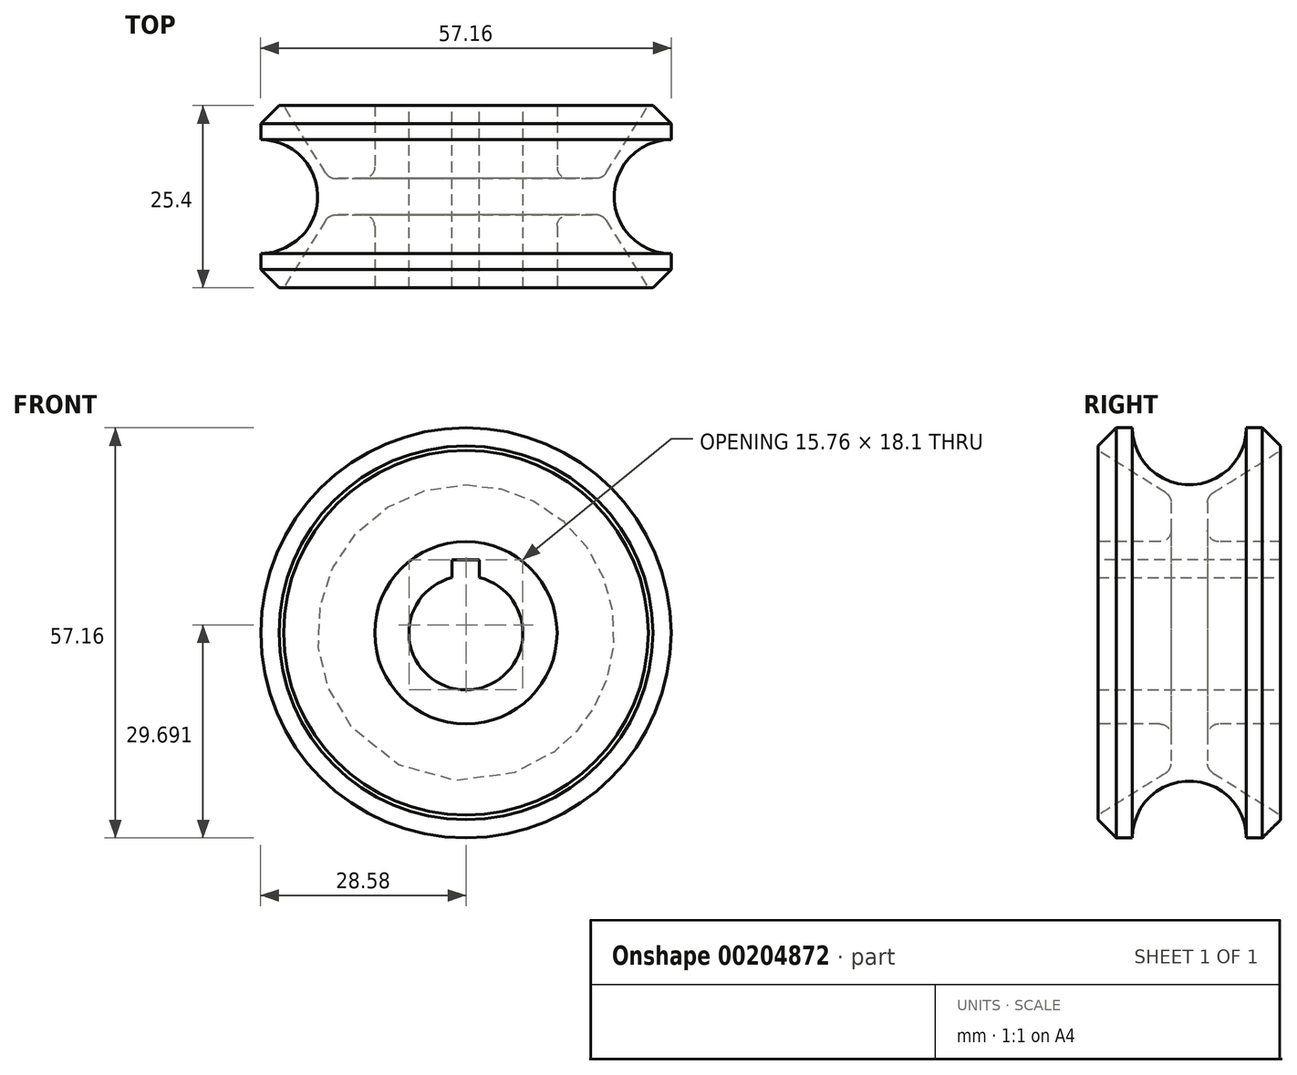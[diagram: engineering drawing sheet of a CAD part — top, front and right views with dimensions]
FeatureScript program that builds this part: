
annotation { "Feature Type Name" : "Feature", "Feature Type Description" : "" }
export const myFeature = defineFeature(function(context is Context, id is Id, definition is map)
    precondition{}
    {
        {
            var Q0;
            Q0=qCreatedBy(makeId("Front.planeOp"),FACE);
            var sketch = newSketch(context, id + "F0", { "sketchPlane" : qUnion([Q0])});
            skCircle(sketch, "E0", {"center": v(0, 0) * mm, "radius": 7.94 * mm});
            skCircle(sketch, "E1", {"center": v(0, 0) * mm, "radius": 28.58 * mm});
            skSolve(sketch);
        }
        {
            var Q0;
            Q0=makeQuery(id+"F0.imprint","IMPRINT",FACE,{"disambiguationData":[TD([[makeQuery(id+"F0.imprint","IMPRINT",EDGE,{"derivedFrom":sQuery(id+"F0.wireOp",EDGE,"E0")}),-1.0]])]});
            extrude(context, id + "F1", {"entities" : qUnion([Q0]), "endBound" : BoundingType.SYMMETRIC, "depth" : 25.4 * mm});
        }
        {
            var Q0;
            Q0=qCreatedBy(makeId("Right.planeOp"),FACE);
            var sketch = newSketch(context, id + "F2", { "sketchPlane" : qUnion([Q0])});
            skCircle(sketch, "E2", {"center": v(0, 28.58) * mm, "radius": 7.94 * mm});
            skLineSegment(sketch, "E3", {"start": v(-58.61, 0) * mm, "end": v(46.92, 0) * mm});
            skSolve(sketch);
        }
        {
            var Q0;
            Q0=makeQuery(id+"F2.imprint","IMPRINT",FACE,{"disambiguationData":[TD([[makeQuery(id+"F2.imprint","IMPRINT",EDGE,{"derivedFrom":sQuery(id+"F2.wireOp",EDGE,"E2")}),1.0]])]});
            var Q1;
            Q1=sQuery(id+"F2.wireOp",EDGE,"E3");
            revolve(context, id + "F3", {"operationType" : NewBodyOperationType.REMOVE, "entities" : qUnion([Q0]), "axis" : qUnion([Q1]), "revolveType" : RevolveType.FULL, "oppositeDirection" : true});
        }
        {
            var Q0;
            Q0=qCreatedBy(makeId("Right.planeOp"),FACE);
            var sketch = newSketch(context, id + "F4", { "sketchPlane" : qUnion([Q0])});
            skLineSegment(sketch, "E4", {"start": v(12.7, 25.4) * mm, "end": v(2.54, 19.05) * mm});
            skLineSegment(sketch, "E5", {"start": v(2.54, 19.05) * mm, "end": v(2.54, 12.7) * mm});
            skLineSegment(sketch, "E6", {"start": v(2.54, 12.7) * mm, "end": v(12.7, 12.7) * mm});
            skLineSegment(sketch, "E7", {"start": v(12.7, 25.4) * mm, "end": v(12.7, 12.7) * mm});
            skLineSegment(sketch, "E8.MirrorCS", {"start": v(-2.54, 19.05) * mm, "end": v(-2.54, 12.7) * mm});
            skLineSegment(sketch, "E9.MirrorCS", {"start": v(-2.54, 12.7) * mm, "end": v(-12.7, 12.7) * mm});
            skLineSegment(sketch, "E10.MirrorCS", {"start": v(-12.7, 25.4) * mm, "end": v(-12.7, 12.7) * mm});
            skLineSegment(sketch, "E11.MirrorCS", {"start": v(-12.7, 25.4) * mm, "end": v(-2.54, 19.05) * mm});
            skSolve(sketch);
        }
        {
            var Q0;
            Q0 = qSketchRegion(id + "F4", true);
            var Q1;
            Q1=sQuery(id+"F2.wireOp",EDGE,"E3");
            revolve(context, id + "F5", {"operationType" : NewBodyOperationType.REMOVE, "entities" : qUnion([Q0]), "axis" : qUnion([Q1]), "revolveType" : RevolveType.FULL});
        }
        {
            var Q0;
            Q0=makeQuery(id+"F5.boolean.opBoolean","COPY",EDGE,{"derivedFrom":makeQuery(id+"F5.opRevolve","SWEPT_EDGE",EDGE,{"disambiguationData":[OSD([sQuery(id+"F4.wireOp",EDGE,"E8.MirrorCS"),sQuery(id+"F4.wireOp",EDGE,"E11.MirrorCS")])]})});
            var Q1;
            Q1=makeQuery(id+"F5.boolean.opBoolean","COPY",EDGE,{"derivedFrom":makeQuery(id+"F5.opRevolve","SWEPT_EDGE",EDGE,{"disambiguationData":[OSD([sQuery(id+"F4.wireOp",EDGE,"E4"),sQuery(id+"F4.wireOp",EDGE,"E5")])]})});
            var Q2;
            Q2=makeQuery(id+"F5.boolean.opBoolean","COPY",EDGE,{"derivedFrom":makeQuery(id+"F5.opRevolve","SWEPT_EDGE",EDGE,{"disambiguationData":[OSD([sQuery(id+"F4.wireOp",EDGE,"E8.MirrorCS"),sQuery(id+"F4.wireOp",EDGE,"E9.MirrorCS")])]})});
            var Q3;
            Q3=makeQuery(id+"F5.boolean.opBoolean","COPY",FACE,{"derivedFrom":makeQuery(id+"F5.opRevolve","SWEPT_FACE",FACE,{"disambiguationData":[OSD([sQuery(id+"F4.wireOp",EDGE,"E5")])]})});
            fillet(context, id + "F6", {"entities" : qUnion([Q0, Q1, Q2, Q3]), "radius" : 1.59 * mm, "tangentPropagation" : true, "allowEdgeOverflow" : false});
        }
        {
            var Q0;
            Q0=makeQuery(id+"F1.opExtrude","CAP_EDGE",EDGE,{"disambiguationData":[OSD([sQuery(id+"F0.wireOp",EDGE,"E1")])],"isStart":true});
            var Q1;
            Q1=makeQuery(id+"F1.opExtrude","CAP_EDGE",EDGE,{"disambiguationData":[OSD([sQuery(id+"F0.wireOp",EDGE,"E1")])],"isStart":false});
            chamfer(context, id + "F7", {"entities" : qUnion([Q0, Q1]), "chamferType" : ChamferType.OFFSET_ANGLE, "width" : 2.54 * mm, "oppositeDirection" : false, "angle" : 45 * degree, "tangentPropagation" : true});
        }
        {
            var Q0;
            Q0=qCreatedBy(makeId("Front.planeOp"),FACE);
            var sketch = newSketch(context, id + "F8", { "sketchPlane" : qUnion([Q0])});
            skLineSegment(sketch, "E12.bottom", {"start": v(1.9, 0) * mm, "end": v(-1.9, 0) * mm});
            skLineSegment(sketch, "E12.top", {"start": v(1.9, 10.16) * mm, "end": v(-1.9, 10.16) * mm});
            skLineSegment(sketch, "E12.left", {"start": v(1.9, 0) * mm, "end": v(1.9, 10.16) * mm});
            skLineSegment(sketch, "E12.right", {"start": v(-1.9, 0) * mm, "end": v(-1.9, 10.16) * mm});
            skSolve(sketch);
        }
        {
            var Q0;
            Q0 = qSketchRegion(id + "F8", true);
            extrude(context, id + "F9", {"entities" : qUnion([Q0]), "operationType" : NewBodyOperationType.REMOVE, "endBound" : BoundingType.SYMMETRIC, "oppositeDirection" : true, "depth" : 25.4 * mm});
        }
    });
